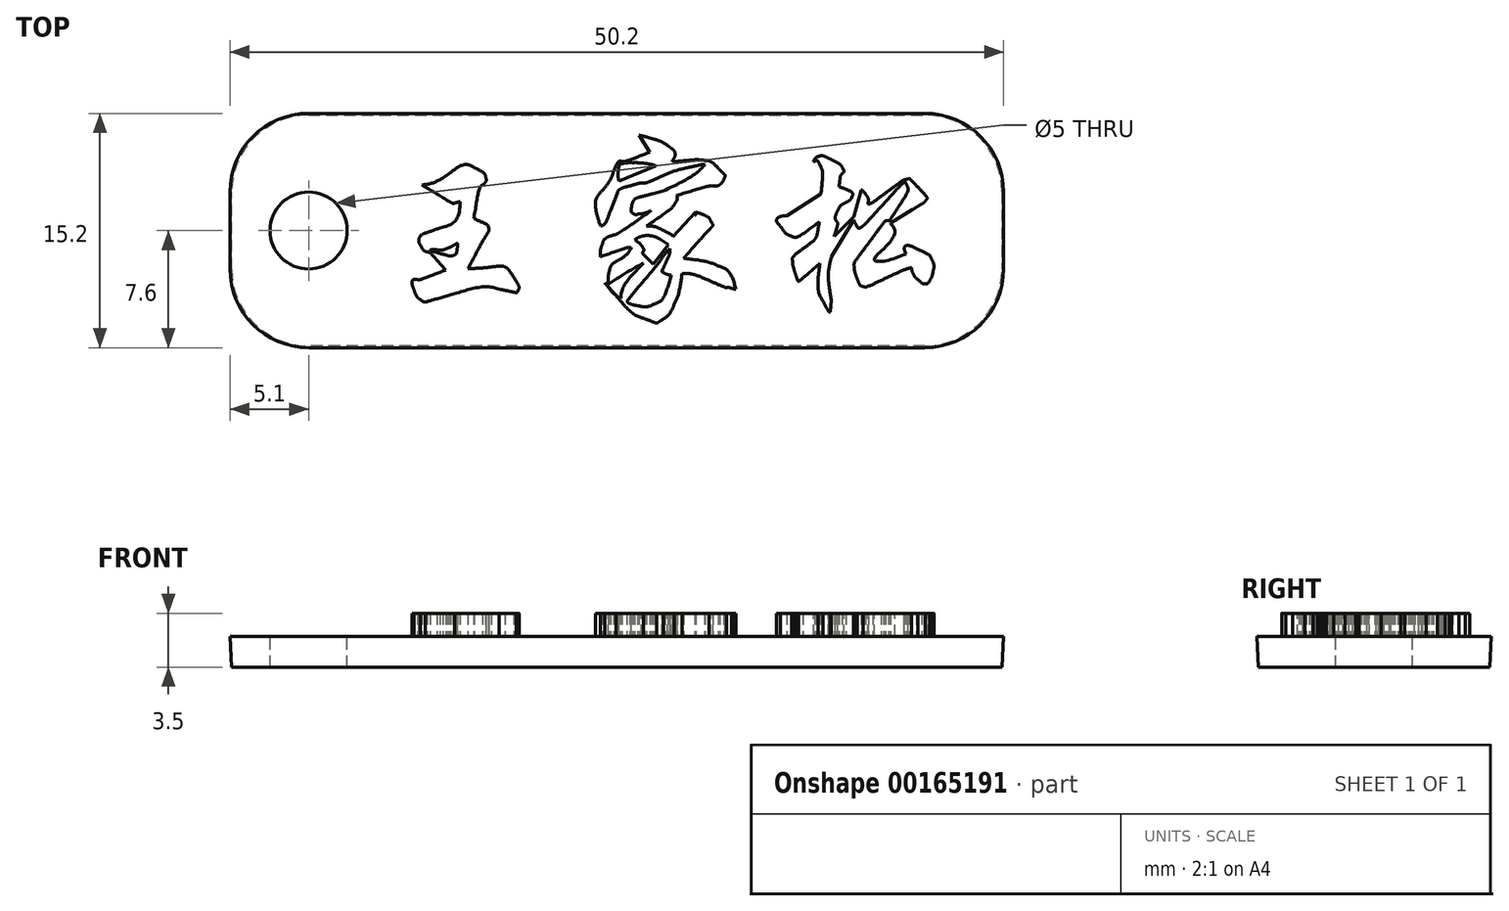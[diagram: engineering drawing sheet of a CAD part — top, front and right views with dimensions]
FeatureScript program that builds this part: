
annotation { "Feature Type Name" : "Feature", "Feature Type Description" : "" }
export const myFeature = defineFeature(function(context is Context, id is Id, definition is map)
    precondition{}
    {
        {
            var Q0;
            Q0=qCreatedBy(makeId("Top.planeOp"),FACE);
            var sketch = newSketch(context, id + "F0", { "sketchPlane" : qUnion([Q0])});
            skLineSegment(sketch, "E0.bottom", {"start": v(20, 7.5) * mm, "end": v(-20, 7.5) * mm});
            skLineSegment(sketch, "E0.top", {"start": v(20, -7.5) * mm, "end": v(-20, -7.5) * mm});
            skLineSegment(sketch, "E0.left", {"start": v(25, 2.5) * mm, "end": v(25, -2.5) * mm});
            skLineSegment(sketch, "E0.right", {"start": v(-25, 2.5) * mm, "end": v(-25, -2.5) * mm});
            skPoint(sketch, "E0.middle", {"position": v(0, 0) * mm});
            skPoint(sketch, "E1.visualSharp", {"position": v(25, 7.5) * mm});
            skArc(sketch, "E1.filletArc", {"start": v(25, 2.5) * mm, "mid": v(23.54, 6.04) * mm, "end": v(20, 7.5) * mm});
            skPoint(sketch, "E2.visualSharp", {"position": v(25, -7.5) * mm});
            skArc(sketch, "E2.filletArc", {"start": v(20, -7.5) * mm, "mid": v(23.54, -6.04) * mm, "end": v(25, -2.5) * mm});
            skPoint(sketch, "E3.visualSharp", {"position": v(-25, 7.5) * mm});
            skArc(sketch, "E3.filletArc", {"start": v(-20, 7.5) * mm, "mid": v(-23.54, 6.04) * mm, "end": v(-25, 2.5) * mm});
            skPoint(sketch, "E4.visualSharp", {"position": v(-25, -7.5) * mm});
            skArc(sketch, "E4.filletArc", {"start": v(-25, -2.5) * mm, "mid": v(-23.54, -6.04) * mm, "end": v(-20, -7.5) * mm});
            skSolve(sketch);
        }
        {
            var Q0;
            Q0=makeQuery(id+"F0.imprint","IMPRINT",FACE,{"disambiguationData":[TD([[makeQuery(id+"F0.imprint","IMPRINT",EDGE,{"derivedFrom":sQuery(id+"F0.wireOp",EDGE,"E0.bottom")}),1.0]])]});
            extrude(context, id + "F1", {"entities" : qUnion([Q0]), "depth" : 2 * mm, "hasDraft" : true, "draftAngle" : 3 * degree});
        }
        {
            var Q0;
            Q0=makeQuery(id+"F1.opExtrude","CAP_FACE",FACE,{"disambiguationData":[OSD([sQuery(id+"F0.wireOp",EDGE,"E0.bottom"),sQuery(id+"F0.wireOp",EDGE,"E0.top"),sQuery(id+"F0.wireOp",EDGE,"E0.left"),sQuery(id+"F0.wireOp",EDGE,"E0.right"),sQuery(id+"F0.wireOp",EDGE,"E1.filletArc"),sQuery(id+"F0.wireOp",EDGE,"E2.filletArc"),sQuery(id+"F0.wireOp",EDGE,"E3.filletArc"),sQuery(id+"F0.wireOp",EDGE,"E4.filletArc")])],"isStart":false});
            var sketch = newSketch(context, id + "F2", { "sketchPlane" : qUnion([Q0])});
            skCircle(sketch, "E5", {"center": v(-20, 0) * mm, "radius": 2.5 * mm});
            skLineSegment(sketch, "E6", {"start": v(-20, 7.6) * mm, "end": v(-20, -7.6) * mm, "construction": true});
            skLineSegment(sketch, "E7", {"start": v(20, -7.6) * mm, "end": v(20, 7.6) * mm, "construction": true});
            skSolve(sketch);
        }
        {
            var Q0;
            Q0=makeQuery(id+"F2.imprint","IMPRINT",FACE,{"disambiguationData":[TD([[makeQuery(id+"F2.imprint","IMPRINT",EDGE,{"derivedFrom":sQuery(id+"F2.wireOp",EDGE,"E5")}),1.0]])]});
            extrude(context, id + "F3", {"entities" : qUnion([Q0]), "operationType" : NewBodyOperationType.REMOVE, "endBound" : BoundingType.THROUGH_ALL, "oppositeDirection" : true, "depth" : 14 * mm});
        }
        {
            var Q0;
            Q0=makeQuery(id+"F2.imprint","IMPRINT",FACE,{"disambiguationData":[TD([[makeQuery(id+"F2.imprint","IMPRINT",EDGE,{"derivedFrom":sQuery(id+"F2.wireOp",EDGE,"E5")}),-1.0]])]});
            var sketch = newSketch(context, id + "F4", { "sketchPlane" : qUnion([Q0])});
            skFitSpline(sketch, "E8", {"points": [v(-6.47, -4.03) * mm, v(-6.47, -4.03) * mm, v(-6.49, -4.03) * mm, v(-6.52, -4.03) * mm, v(-6.47, -4.03) * mm]});
            skFitSpline(sketch, "E9", {"points": [v(-6.52, -4.03) * mm, v(-6.56, -4.03) * mm, v(-6.93, -3.95) * mm, v(-7.65, -3.8) * mm]});
            skFitSpline(sketch, "E10", {"points": [v(-7.65, -3.8) * mm, v(-8.35, -3.65) * mm, v(-9.3, -3.75) * mm, v(-10.53, -4.1) * mm]});
            skFitSpline(sketch, "E11", {"points": [v(-10.53, -4.1) * mm, v(-11.75, -4.45) * mm, v(-12.4, -4.63) * mm, v(-12.44, -4.63) * mm]});
            skFitSpline(sketch, "E12", {"points": [v(-12.44, -4.63) * mm, v(-12.52, -4.63) * mm, v(-12.62, -4.58) * mm, v(-12.75, -4.48) * mm]});
            skFitSpline(sketch, "E13", {"points": [v(-12.75, -4.48) * mm, v(-12.9, -4.37) * mm, v(-13.04, -4.17) * mm, v(-13.15, -3.87) * mm]});
            skFitSpline(sketch, "E14", {"points": [v(-13.15, -3.87) * mm, v(-13.27, -3.56) * mm, v(-13.3, -3.32) * mm, v(-13.22, -3.17) * mm]});
            skFitSpline(sketch, "E15", {"points": [v(-13.22, -3.17) * mm, v(-13.12, -3.17) * mm, v(-13.03, -3.18) * mm, v(-12.94, -3.18) * mm]});
            skFitSpline(sketch, "E16", {"points": [v(-12.94, -3.18) * mm, v(-12.82, -3.2) * mm, v(-12.21, -2.99) * mm, v(-11.1, -2.57) * mm]});
            skFitSpline(sketch, "E17", {"points": [v(-11.1, -2.57) * mm, v(-11.78, -1.8) * mm, v(-12.18, -1.4) * mm, v(-12.3, -1.38) * mm]});
            skFitSpline(sketch, "E18", {"points": [v(-12.3, -1.38) * mm, v(-12.44, -1.35) * mm, v(-12.57, -1.24) * mm, v(-12.69, -1.05) * mm]});
            skFitSpline(sketch, "E19", {"points": [v(-12.69, -1.05) * mm, v(-12.8, -0.86) * mm, v(-12.85, -0.73) * mm, v(-12.85, -0.65) * mm]});
            skFitSpline(sketch, "E20", {"points": [v(-12.85, -0.65) * mm, v(-12.85, -0.57) * mm, v(-12.83, -0.5) * mm, v(-12.78, -0.4) * mm]});
            skFitSpline(sketch, "E21", {"points": [v(-12.78, -0.4) * mm, v(-12.7, -0.3) * mm, v(-12.28, -0.11) * mm, v(-11.49, 0.17) * mm]});
            skFitSpline(sketch, "E22", {"points": [v(-11.49, 0.17) * mm, v(-10.7, 0.43) * mm, v(-10.27, 1) * mm, v(-10.18, 1.88) * mm]});
            skFitSpline(sketch, "E23", {"points": [v(-10.18, 1.88) * mm, v(-10.44, 1.8) * mm, v(-10.6, 1.77) * mm, v(-10.63, 1.77) * mm]});
            skFitSpline(sketch, "E24", {"points": [v(-10.63, 1.77) * mm, v(-10.65, 1.77) * mm, v(-11.33, 2.16) * mm, v(-12.65, 2.96) * mm]});
            skFitSpline(sketch, "E25", {"points": [v(-12.65, 2.96) * mm, v(-12.08, 3.05) * mm, v(-11.47, 3.3) * mm, v(-10.82, 3.74) * mm]});
            skFitSpline(sketch, "E26", {"points": [v(-10.82, 3.74) * mm, v(-10.2, 4.17) * mm, v(-9.69, 4.29) * mm, v(-9.26, 4.08) * mm]});
            skFitSpline(sketch, "E27", {"points": [v(-9.26, 4.08) * mm, v(-8.82, 3.87) * mm, v(-8.56, 3.66) * mm, v(-8.5, 3.47) * mm]});
            skFitSpline(sketch, "E28", {"points": [v(-8.5, 3.47) * mm, v(-8.47, 3.28) * mm, v(-8.54, 3.11) * mm, v(-8.7, 2.97) * mm]});
            skFitSpline(sketch, "E29", {"points": [v(-8.7, 2.97) * mm, v(-8.86, 2.83) * mm, v(-9.06, 2.1) * mm, v(-9.29, 0.78) * mm]});
            skFitSpline(sketch, "E30", {"points": [v(-9.29, 0.78) * mm, v(-8.67, 0.5) * mm, v(-8.35, 0.33) * mm, v(-8.33, 0.23) * mm]});
            skFitSpline(sketch, "E31", {"points": [v(-8.33, 0.23) * mm, v(-8.3, 0.13) * mm, v(-8.29, 0.07) * mm, v(-8.29, 0.04) * mm]});
            skFitSpline(sketch, "E32", {"points": [v(-8.29, 0.04) * mm, v(-8.29, 0) * mm, v(-8.36, -0.14) * mm, v(-8.52, -0.38) * mm]});
            skFitSpline(sketch, "E33", {"points": [v(-8.52, -0.38) * mm, v(-8.65, -0.6) * mm, v(-9.04, -1.3) * mm, v(-9.67, -2.48) * mm]});
            skFitSpline(sketch, "E34", {"points": [v(-9.67, -2.48) * mm, v(-9, -2.45) * mm, v(-8.5, -2.4) * mm, v(-8.16, -2.36) * mm]});
            skFitSpline(sketch, "E35", {"points": [v(-8.16, -2.36) * mm, v(-7.68, -2.31) * mm, v(-7.38, -2.31) * mm, v(-7.26, -2.36) * mm]});
            skFitSpline(sketch, "E36", {"points": [v(-7.26, -2.36) * mm, v(-7.14, -2.42) * mm, v(-6.94, -2.65) * mm, v(-6.69, -3.04) * mm]});
            skFitSpline(sketch, "E37", {"points": [v(-6.69, -3.04) * mm, v(-6.44, -3.44) * mm, v(-6.34, -3.7) * mm, v(-6.38, -3.82) * mm]});
            skFitSpline(sketch, "E38", {"points": [v(-6.38, -3.82) * mm, v(-6.44, -3.96) * mm, v(-6.49, -4.03) * mm, v(-6.52, -4.03) * mm]});
            skFitSpline(sketch, "E39", {"points": [v(-10.8, -1.09) * mm, v(-10.8, -1.09) * mm, v(-10.86, -1.1) * mm, v(-10.97, -1.15) * mm, v(-10.8, -1.09) * mm]});
            skLineSegment(sketch, "E40", {"start": v(-6.52, -4.03) * mm, "end": v(-6.47, -4.03) * mm});
            skFitSpline(sketch, "E41", {"points": [v(-11.68, -1.25) * mm, v(-11.9, -1.23) * mm, v(-12.05, -1.24) * mm, v(-12.12, -1.3) * mm]});
            skFitSpline(sketch, "E42", {"points": [v(-12.12, -1.3) * mm, v(-11.3, -1.53) * mm, v(-10.86, -1.65) * mm, v(-10.8, -1.65) * mm]});
            skFitSpline(sketch, "E43", {"points": [v(-10.8, -1.65) * mm, v(-10.72, -1.65) * mm, v(-10.59, -1.6) * mm, v(-10.41, -1.52) * mm]});
            skFitSpline(sketch, "E44", {"points": [v(-10.41, -1.52) * mm, v(-10.36, -1.17) * mm, v(-10.34, -0.94) * mm, v(-10.35, -0.82) * mm]});
            skFitSpline(sketch, "E45", {"points": [v(-10.35, -0.82) * mm, v(-10.65, -1) * mm, v(-10.86, -1.1) * mm, v(-10.97, -1.15) * mm]});
            skLineSegment(sketch, "E46", {"start": v(-10.97, -1.15) * mm, "end": v(-11.28, -1.28) * mm});
            skLineSegment(sketch, "E47", {"start": v(-11.28, -1.28) * mm, "end": v(-11.68, -1.25) * mm});
            skLineSegment(sketch, "E48", {"start": v(-11.68, -1.25) * mm, "end": v(-10.97, -1.15) * mm});
            skFitSpline(sketch, "E49", {"points": [v(7.6, -3.8) * mm, v(7.6, -3.8) * mm, v(7.54, -3.78) * mm, v(7.43, -3.75) * mm, v(7.6, -3.8) * mm]});
            skFitSpline(sketch, "E50", {"points": [v(7.43, -3.75) * mm, v(7.3, -3.7) * mm, v(7.2, -3.7) * mm, v(7.12, -3.7) * mm]});
            skFitSpline(sketch, "E51", {"points": [v(7.12, -3.7) * mm, v(7.1, -3.7) * mm, v(6.71, -3.55) * mm, v(5.99, -3.25) * mm]});
            skFitSpline(sketch, "E52", {"points": [v(5.99, -3.25) * mm, v(5.3, -2.95) * mm, v(4.72, -2.8) * mm, v(4.23, -2.8) * mm]});
            skFitSpline(sketch, "E53", {"points": [v(4.23, -2.8) * mm, v(4.1, -3.66) * mm, v(3.94, -4.32) * mm, v(3.74, -4.77) * mm]});
            skFitSpline(sketch, "E54", {"points": [v(3.74, -4.77) * mm, v(3.53, -5.22) * mm, v(3.3, -5.54) * mm, v(3.03, -5.73) * mm]});
            skFitSpline(sketch, "E55", {"points": [v(3.03, -5.73) * mm, v(2.77, -5.9) * mm, v(2.62, -6) * mm, v(2.58, -6) * mm]});
            skFitSpline(sketch, "E56", {"points": [v(2.58, -6) * mm, v(2.55, -6) * mm, v(2.26, -5.9) * mm, v(1.73, -5.7) * mm]});
            skFitSpline(sketch, "E57", {"points": [v(1.73, -5.7) * mm, v(1.23, -5.5) * mm, v(0.64, -5.01) * mm, v(-0.05, -4.22) * mm]});
            skFitSpline(sketch, "E58", {"points": [v(-0.05, -4.22) * mm, v(-0.2, -4.1) * mm, v(-0.43, -3.82) * mm, v(-0.77, -3.4) * mm]});
            skFitSpline(sketch, "E59", {"points": [v(-0.77, -3.4) * mm, v(-0.43, -3.8) * mm, v(-0.18, -4.06) * mm, v(-0.04, -4.2) * mm]});
            skFitSpline(sketch, "E60", {"points": [v(-0.04, -4.2) * mm, v(0.06, -4.3) * mm, v(0.16, -4.36) * mm, v(0.24, -4.4) * mm]});
            skFitSpline(sketch, "E61", {"points": [v(0.24, -4.4) * mm, v(0.37, -3.8) * mm, v(0.87, -3.03) * mm, v(1.74, -2.1) * mm]});
            skFitSpline(sketch, "E62", {"points": [v(1.74, -2.1) * mm, v(0.97, -2.53) * mm, v(0.2, -3) * mm, v(-0.56, -3.5) * mm]});
            skFitSpline(sketch, "E63", {"points": [v(-0.56, -3.5) * mm, v(-0.56, -3.12) * mm, v(-0.53, -2.8) * mm, v(-0.46, -2.54) * mm]});
            skFitSpline(sketch, "E64", {"points": [v(-0.46, -2.54) * mm, v(-0.4, -2.31) * mm, v(-0.2, -2.1) * mm, v(0.14, -1.9) * mm]});
            skFitSpline(sketch, "E65", {"points": [v(0.14, -1.9) * mm, v(0.47, -1.7) * mm, v(0.74, -1.43) * mm, v(0.95, -1.1) * mm]});
            skFitSpline(sketch, "E66", {"points": [v(0.95, -1.1) * mm, v(0.76, -1.1) * mm, v(0.1, -1.3) * mm, v(-1.06, -1.7) * mm]});
            skFitSpline(sketch, "E67", {"points": [v(-1.06, -1.7) * mm, v(-1.06, -1.35) * mm, v(-1.01, -1.06) * mm, v(-0.92, -0.84) * mm]});
            skFitSpline(sketch, "E68", {"points": [v(-0.92, -0.84) * mm, v(-0.84, -0.61) * mm, v(-0.61, -0.43) * mm, v(-0.26, -0.3) * mm]});
            skFitSpline(sketch, "E69", {"points": [v(-0.26, -0.3) * mm, v(0.06, -0.19) * mm, v(0.9, 0.35) * mm, v(2.24, 1.3) * mm]});
            skFitSpline(sketch, "E70", {"points": [v(2.24, 1.3) * mm, v(1.92, 1.17) * mm, v(1.71, 1.1) * mm, v(1.6, 1.09) * mm]});
            skFitSpline(sketch, "E71", {"points": [v(1.6, 1.09) * mm, v(1.51, 1.09) * mm, v(1.43, 1.08) * mm, v(1.34, 1.06) * mm]});
            skFitSpline(sketch, "E72", {"points": [v(1.34, 1.06) * mm, v(1.28, 1.03) * mm, v(1.2, 1.04) * mm, v(1.09, 1.09) * mm]});
            skFitSpline(sketch, "E73", {"points": [v(1.09, 1.09) * mm, v(0.98, 1.16) * mm, v(0.93, 1.24) * mm, v(0.95, 1.34) * mm]});
            skFitSpline(sketch, "E74", {"points": [v(0.95, 1.34) * mm, v(0.95, 1.45) * mm, v(0.96, 1.57) * mm, v(0.99, 1.7) * mm]});
            skFitSpline(sketch, "E75", {"points": [v(0.99, 1.7) * mm, v(1.03, 1.83) * mm, v(1.08, 1.93) * mm, v(1.14, 2) * mm]});
            skFitSpline(sketch, "E76", {"points": [v(1.14, 2) * mm, v(1.2, 2.08) * mm, v(1.6, 2.2) * mm, v(2.34, 2.4) * mm]});
            skLineSegment(sketch, "E77", {"start": v(-10.97, -1.15) * mm, "end": v(-10.8, -1.09) * mm});
            skFitSpline(sketch, "E78", {"points": [v(3.04, 2.58) * mm, v(4.32, 3.2) * mm, v(5.22, 3.78) * mm, v(5.73, 4.3) * mm]});
            skFitSpline(sketch, "E79", {"points": [v(5.73, 4.3) * mm, v(5.64, 4.3) * mm, v(5.27, 4.23) * mm, v(4.64, 4.1) * mm]});
            skFitSpline(sketch, "E80", {"points": [v(4.64, 4.1) * mm, v(4, 3.94) * mm, v(3.4, 3.74) * mm, v(2.84, 3.5) * mm]});
            skFitSpline(sketch, "E81", {"points": [v(2.84, 3.5) * mm, v(2.25, 3.23) * mm, v(1.88, 3.1) * mm, v(1.73, 3.1) * mm]});
            skFitSpline(sketch, "E82", {"points": [v(1.73, 3.1) * mm, v(1.6, 3.1) * mm, v(1.3, 3.03) * mm, v(0.83, 2.9) * mm]});
            skFitSpline(sketch, "E83", {"points": [v(0.83, 2.9) * mm, v(0.37, 2.76) * mm, v(0.1, 2.61) * mm, v(0.04, 2.44) * mm]});
            skLineSegment(sketch, "E84", {"start": v(2.34, 2.4) * mm, "end": v(3.04, 2.58) * mm});
            skLineSegment(sketch, "E85", {"start": v(3.04, 2.58) * mm, "end": v(2.34, 2.4) * mm});
            skFitSpline(sketch, "E86", {"points": [v(-0.4, 1.3) * mm, v(-0.64, 0.7) * mm, v(-0.85, 0.36) * mm, v(-1.05, 0.3) * mm]});
            skFitSpline(sketch, "E87", {"points": [v(-1.05, 0.3) * mm, v(-1.24, 0.87) * mm, v(-1.36, 1.32) * mm, v(-1.38, 1.65) * mm]});
            skFitSpline(sketch, "E88", {"points": [v(-1.38, 1.65) * mm, v(-1.38, 1.94) * mm, v(-1.22, 2.27) * mm, v(-0.9, 2.65) * mm]});
            skFitSpline(sketch, "E89", {"points": [v(-0.9, 2.65) * mm, v(-0.6, 3.02) * mm, v(-0.37, 3.42) * mm, v(-0.2, 3.84) * mm]});
            skFitSpline(sketch, "E90", {"points": [v(-0.2, 3.84) * mm, v(-0.02, 4.27) * mm, v(0.15, 4.5) * mm, v(0.33, 4.5) * mm]});
            skFitSpline(sketch, "E91", {"points": [v(0.33, 4.5) * mm, v(0.53, 4.5) * mm, v(1.13, 4.7) * mm, v(2.14, 5.1) * mm]});
            skLineSegment(sketch, "E92", {"start": v(0.04, 2.44) * mm, "end": v(-0.4, 1.3) * mm});
            skLineSegment(sketch, "E93", {"start": v(-0.4, 1.3) * mm, "end": v(0.04, 2.44) * mm});
            skFitSpline(sketch, "E94", {"points": [v(1.43, 6.2) * mm, v(1.8, 6.1) * mm, v(2.1, 6.02) * mm, v(2.37, 5.94) * mm]});
            skFitSpline(sketch, "E95", {"points": [v(2.37, 5.94) * mm, v(2.7, 5.85) * mm, v(3.01, 5.7) * mm, v(3.31, 5.5) * mm]});
            skFitSpline(sketch, "E96", {"points": [v(3.31, 5.5) * mm, v(3.6, 5.3) * mm, v(3.75, 5.14) * mm, v(3.77, 5.04) * mm]});
            skFitSpline(sketch, "E97", {"points": [v(3.77, 5.04) * mm, v(3.8, 4.95) * mm, v(3.75, 4.76) * mm, v(3.6, 4.5) * mm]});
            skLineSegment(sketch, "E98", {"start": v(2.14, 5.1) * mm, "end": v(1.43, 6.2) * mm});
            skLineSegment(sketch, "E99", {"start": v(1.43, 6.2) * mm, "end": v(2.14, 5.1) * mm});
            skFitSpline(sketch, "E100", {"points": [v(5.08, 4.6) * mm, v(5.28, 4.6) * mm, v(5.49, 4.58) * mm, v(5.7, 4.55) * mm]});
            skFitSpline(sketch, "E101", {"points": [v(5.7, 4.55) * mm, v(5.97, 4.53) * mm, v(6.27, 4.36) * mm, v(6.59, 4.04) * mm]});
            skFitSpline(sketch, "E102", {"points": [v(6.59, 4.04) * mm, v(6.89, 3.74) * mm, v(7.04, 3.58) * mm, v(7.04, 3.56) * mm]});
            skFitSpline(sketch, "E103", {"points": [v(7.04, 3.56) * mm, v(7.04, 3.53) * mm, v(7, 3.44) * mm, v(6.93, 3.29) * mm]});
            skFitSpline(sketch, "E104", {"points": [v(6.93, 3.29) * mm, v(6.87, 3.18) * mm, v(6.8, 3.08) * mm, v(6.7, 2.98) * mm]});
            skFitSpline(sketch, "E105", {"points": [v(6.7, 2.98) * mm, v(6.59, 2.91) * mm, v(6.44, 2.89) * mm, v(6.24, 2.9) * mm]});
            skFitSpline(sketch, "E106", {"points": [v(6.24, 2.9) * mm, v(6.06, 2.9) * mm, v(5.28, 2.7) * mm, v(3.9, 2.3) * mm]});
            skFitSpline(sketch, "E107", {"points": [v(3.9, 2.3) * mm, v(3.93, 2.2) * mm, v(3.94, 2.14) * mm, v(3.93, 2.09) * mm]});
            skFitSpline(sketch, "E108", {"points": [v(3.93, 2.09) * mm, v(3.93, 2.03) * mm, v(3.86, 1.9) * mm, v(3.74, 1.7) * mm]});
            skFitSpline(sketch, "E109", {"points": [v(3.74, 1.7) * mm, v(3.62, 1.51) * mm, v(3.01, 1.05) * mm, v(1.93, 0.3) * mm]});
            skFitSpline(sketch, "E110", {"points": [v(1.93, 0.3) * mm, v(2.26, 0.3) * mm, v(2.62, 0.2) * mm, v(3.03, 0) * mm]});
            skFitSpline(sketch, "E111", {"points": [v(3.03, 0) * mm, v(3.43, -0.2) * mm, v(3.63, -0.34) * mm, v(3.63, -0.4) * mm]});
            skLineSegment(sketch, "E112", {"start": v(3.6, 4.5) * mm, "end": v(5.08, 4.6) * mm});
            skLineSegment(sketch, "E113", {"start": v(5.08, 4.6) * mm, "end": v(3.6, 4.5) * mm});
            skFitSpline(sketch, "E114", {"points": [v(5.13, 1.2) * mm, v(5.68, 1) * mm, v(6, 0.82) * mm, v(6.08, 0.65) * mm]});
            skFitSpline(sketch, "E115", {"points": [v(6.08, 0.65) * mm, v(6.14, 0.54) * mm, v(6.2, 0.44) * mm, v(6.24, 0.36) * mm]});
            skFitSpline(sketch, "E116", {"points": [v(6.24, 0.36) * mm, v(6.24, 0.33) * mm, v(6.16, 0.23) * mm, v(5.99, 0.04) * mm]});
            skFitSpline(sketch, "E117", {"points": [v(5.99, 0.04) * mm, v(5.82, -0.12) * mm, v(5.27, -0.74) * mm, v(4.34, -1.8) * mm]});
            skFitSpline(sketch, "E118", {"points": [v(4.34, -1.8) * mm, v(5.34, -1.93) * mm, v(6.1, -2.1) * mm, v(6.59, -2.3) * mm]});
            skFitSpline(sketch, "E119", {"points": [v(6.59, -2.3) * mm, v(7.1, -2.5) * mm, v(7.47, -3) * mm, v(7.73, -3.8) * mm]});
            skFitSpline(sketch, "E120", {"points": [v(7.73, -3.8) * mm, v(7.64, -3.8) * mm, v(7.54, -3.78) * mm, v(7.43, -3.75) * mm]});
            skLineSegment(sketch, "E121", {"start": v(3.63, -0.4) * mm, "end": v(5.13, 1.2) * mm});
            skLineSegment(sketch, "E122", {"start": v(5.13, 1.2) * mm, "end": v(3.63, -0.4) * mm});
            skFitSpline(sketch, "E123", {"points": [v(2.53, 4.2) * mm, v(2.35, 4.26) * mm, v(2.13, 4.32) * mm, v(1.88, 4.35) * mm]});
            skFitSpline(sketch, "E124", {"points": [v(1.88, 4.35) * mm, v(1.68, 4.38) * mm, v(1.4, 4.4) * mm, v(1.04, 4.4) * mm]});
            skFitSpline(sketch, "E125", {"points": [v(1.04, 4.4) * mm, v(0.73, 4.4) * mm, v(0.43, 4.37) * mm, v(0.13, 4.3) * mm]});
            skFitSpline(sketch, "E126", {"points": [v(0.13, 4.3) * mm, v(0.13, 4.12) * mm, v(0.12, 3.97) * mm, v(0.1, 3.85) * mm]});
            skFitSpline(sketch, "E127", {"points": [v(0.1, 3.85) * mm, v(0.07, 3.75) * mm, v(0.08, 3.53) * mm, v(0.14, 3.2) * mm]});
            skLineSegment(sketch, "E128", {"start": v(7.43, -3.75) * mm, "end": v(7.6, -3.8) * mm});
            skFitSpline(sketch, "E129", {"points": [v(5.14, 1) * mm, v(5.14, 1) * mm, v(5.13, 1) * mm, v(5.1, 1) * mm, v(5.14, 1) * mm]});
            skFitSpline(sketch, "E130", {"points": [v(5.1, 1) * mm, v(5.06, 1) * mm, v(4.84, 0.76) * mm, v(4.44, 0.28) * mm]});
            skFitSpline(sketch, "E131", {"points": [v(4.44, 0.28) * mm, v(4.05, -0.18) * mm, v(3.86, -0.47) * mm, v(3.89, -0.6) * mm]});
            skFitSpline(sketch, "E132", {"points": [v(3.89, -0.6) * mm, v(3.93, -0.74) * mm, v(3.98, -0.83) * mm, v(4.04, -0.9) * mm]});
            skFitSpline(sketch, "E133", {"points": [v(4.04, -0.9) * mm, v(4.57, -0.5) * mm, v(4.92, -0.12) * mm, v(5.1, 0.24) * mm]});
            skFitSpline(sketch, "E134", {"points": [v(5.1, 0.24) * mm, v(5.26, 0.61) * mm, v(5.31, 0.83) * mm, v(5.24, 0.9) * mm]});
            skFitSpline(sketch, "E135", {"points": [v(5.24, 0.9) * mm, v(5.18, 0.96) * mm, v(5.13, 1) * mm, v(5.1, 1) * mm]});
            skLineSegment(sketch, "E136", {"start": v(0.14, 3.2) * mm, "end": v(2.53, 4.2) * mm});
            skLineSegment(sketch, "E137", {"start": v(2.53, 4.2) * mm, "end": v(0.14, 3.2) * mm});
            skFitSpline(sketch, "E138", {"points": [v(3.35, -0.9) * mm, v(2.55, -0.44) * mm, v(1.82, -0.33) * mm, v(1.15, -0.59) * mm]});
            skFitSpline(sketch, "E139", {"points": [v(1.15, -0.59) * mm, v(1.42, -0.8) * mm, v(1.6, -0.95) * mm, v(1.65, -1.05) * mm]});
            skFitSpline(sketch, "E140", {"points": [v(1.65, -1.05) * mm, v(1.72, -1.16) * mm, v(1.75, -1.22) * mm, v(1.75, -1.24) * mm]});
            skFitSpline(sketch, "E141", {"points": [v(1.75, -1.24) * mm, v(1.75, -1.27) * mm, v(1.72, -1.36) * mm, v(1.65, -1.5) * mm]});
            skLineSegment(sketch, "E142", {"start": v(5.1, 1) * mm, "end": v(5.14, 1) * mm});
            skFitSpline(sketch, "E143", {"points": [v(3.38, -2.89) * mm, v(3.38, -2.89) * mm, v(3.3, -2.86) * mm, v(3.13, -2.79) * mm, v(3.38, -2.89) * mm]});
            skFitSpline(sketch, "E144", {"points": [v(3.13, -2.79) * mm, v(3, -2.72) * mm, v(2.94, -2.67) * mm, v(2.94, -2.65) * mm]});
            skFitSpline(sketch, "E145", {"points": [v(2.94, -2.65) * mm, v(2.94, -2.61) * mm, v(3.03, -2.41) * mm, v(3.2, -2.05) * mm]});
            skFitSpline(sketch, "E146", {"points": [v(3.2, -2.05) * mm, v(3.37, -1.66) * mm, v(3.45, -1.37) * mm, v(3.45, -1.18) * mm]});
            skFitSpline(sketch, "E147", {"points": [v(3.45, -1.18) * mm, v(3.23, -1.4) * mm, v(3.06, -1.6) * mm, v(2.94, -1.78) * mm]});
            skFitSpline(sketch, "E148", {"points": [v(2.94, -1.78) * mm, v(2.78, -2.02) * mm, v(2.02, -2.95) * mm, v(0.65, -4.6) * mm]});
            skFitSpline(sketch, "E149", {"points": [v(0.65, -4.6) * mm, v(0.78, -4.72) * mm, v(1.03, -4.82) * mm, v(1.4, -4.88) * mm]});
            skFitSpline(sketch, "E150", {"points": [v(1.4, -4.88) * mm, v(1.77, -4.95) * mm, v(2.14, -4.9) * mm, v(2.5, -4.73) * mm]});
            skFitSpline(sketch, "E151", {"points": [v(2.5, -4.73) * mm, v(2.86, -4.57) * mm, v(3.21, -3.96) * mm, v(3.54, -2.89) * mm]});
            skFitSpline(sketch, "E152", {"points": [v(3.54, -2.89) * mm, v(3.43, -2.89) * mm, v(3.3, -2.86) * mm, v(3.13, -2.79) * mm]});
            skLineSegment(sketch, "E153", {"start": v(1.65, -1.5) * mm, "end": v(2.35, -2.2) * mm});
            skLineSegment(sketch, "E154", {"start": v(2.35, -2.2) * mm, "end": v(3.35, -0.9) * mm});
            skLineSegment(sketch, "E155", {"start": v(3.35, -0.9) * mm, "end": v(1.65, -1.5) * mm});
            skFitSpline(sketch, "E156", {"points": [v(20.45, -3.02) * mm, v(20.45, -3.02) * mm, v(20.4, -3.1) * mm, v(20.31, -3.25) * mm, v(20.45, -3.02) * mm]});
            skFitSpline(sketch, "E157", {"points": [v(20.31, -3.25) * mm, v(20.22, -3.4) * mm, v(20.12, -3.46) * mm, v(20.02, -3.46) * mm]});
            skFitSpline(sketch, "E158", {"points": [v(20.02, -3.46) * mm, v(19.92, -3.46) * mm, v(19.76, -3.37) * mm, v(19.54, -3.18) * mm]});
            skFitSpline(sketch, "E159", {"points": [v(19.54, -3.18) * mm, v(19.34, -2.99) * mm, v(19.2, -2.73) * mm, v(19.12, -2.4) * mm]});
            skFitSpline(sketch, "E160", {"points": [v(19.12, -2.4) * mm, v(18.82, -2.49) * mm, v(18.24, -2.73) * mm, v(17.4, -3.12) * mm]});
            skFitSpline(sketch, "E161", {"points": [v(17.4, -3.12) * mm, v(16.6, -3.5) * mm, v(16.13, -3.67) * mm, v(15.99, -3.63) * mm]});
            skFitSpline(sketch, "E162", {"points": [v(15.99, -3.63) * mm, v(15.85, -3.6) * mm, v(15.72, -3.44) * mm, v(15.6, -3.15) * mm]});
            skFitSpline(sketch, "E163", {"points": [v(15.6, -3.15) * mm, v(15.5, -2.85) * mm, v(15.43, -2.6) * mm, v(15.41, -2.42) * mm]});
            skFitSpline(sketch, "E164", {"points": [v(15.41, -2.42) * mm, v(15.4, -2.2) * mm, v(15.45, -2.02) * mm, v(15.58, -1.85) * mm]});
            skFitSpline(sketch, "E165", {"points": [v(15.58, -1.85) * mm, v(15.78, -1.57) * mm, v(16.12, -1.1) * mm, v(16.62, -0.45) * mm]});
            skFitSpline(sketch, "E166", {"points": [v(16.62, -0.45) * mm, v(17.18, 0.32) * mm, v(17.52, 0.66) * mm, v(17.65, 0.56) * mm]});
            skFitSpline(sketch, "E167", {"points": [v(17.65, 0.56) * mm, v(18.52, 1.9) * mm, v(18.92, 2.67) * mm, v(18.84, 2.88) * mm]});
            skFitSpline(sketch, "E168", {"points": [v(18.84, 2.88) * mm, v(18.76, 3.08) * mm, v(18.7, 3.15) * mm, v(18.62, 3.1) * mm]});
            skFitSpline(sketch, "E169", {"points": [v(18.62, 3.1) * mm, v(18.55, 3.07) * mm, v(18.06, 2.55) * mm, v(17.15, 1.55) * mm]});
            skFitSpline(sketch, "E170", {"points": [v(17.15, 1.55) * mm, v(16.23, 0.54) * mm, v(15.7, 0.15) * mm, v(15.55, 0.36) * mm]});
            skFitSpline(sketch, "E171", {"points": [v(15.55, 0.36) * mm, v(15.47, 0.49) * mm, v(15.41, 0.6) * mm, v(15.39, 0.7) * mm]});
            skLineSegment(sketch, "E172", {"start": v(3.13, -2.79) * mm, "end": v(3.38, -2.89) * mm});
            skFitSpline(sketch, "E173", {"points": [v(13.93, -1.7) * mm, v(13.8, -2.3) * mm, v(13.73, -2.75) * mm, v(13.74, -3.06) * mm]});
            skFitSpline(sketch, "E174", {"points": [v(13.74, -3.06) * mm, v(13.75, -3.31) * mm, v(13.78, -3.6) * mm, v(13.84, -3.95) * mm]});
            skLineSegment(sketch, "E175", {"start": v(15.39, 0.7) * mm, "end": v(13.93, -1.7) * mm});
            skLineSegment(sketch, "E176", {"start": v(13.93, -1.7) * mm, "end": v(15.39, 0.7) * mm});
            skFitSpline(sketch, "E177", {"points": [v(13.87, -5.3) * mm, v(13.8, -5.3) * mm, v(13.64, -5.05) * mm, v(13.38, -4.56) * mm]});
            skFitSpline(sketch, "E178", {"points": [v(13.38, -4.56) * mm, v(13.12, -4.08) * mm, v(13.06, -3.26) * mm, v(13.19, -2.12) * mm]});
            skFitSpline(sketch, "E179", {"points": [v(13.19, -2.12) * mm, v(12.28, -2.9) * mm, v(11.82, -3.3) * mm, v(11.8, -3.3) * mm]});
            skFitSpline(sketch, "E180", {"points": [v(11.8, -3.3) * mm, v(11.77, -3.3) * mm, v(11.7, -3.12) * mm, v(11.58, -2.76) * mm]});
            skFitSpline(sketch, "E181", {"points": [v(11.58, -2.76) * mm, v(11.46, -2.38) * mm, v(11.4, -2.11) * mm, v(11.4, -1.97) * mm]});
            skFitSpline(sketch, "E182", {"points": [v(11.4, -1.97) * mm, v(11.4, -1.79) * mm, v(11.62, -1.53) * mm, v(12.09, -1.18) * mm]});
            skFitSpline(sketch, "E183", {"points": [v(12.09, -1.18) * mm, v(12.57, -0.83) * mm, v(12.84, -0.6) * mm, v(12.9, -0.48) * mm]});
            skFitSpline(sketch, "E184", {"points": [v(12.9, -0.48) * mm, v(12.97, -0.4) * mm, v(13.05, -0.04) * mm, v(13.15, 0.58) * mm]});
            skFitSpline(sketch, "E185", {"points": [v(13.15, 0.58) * mm, v(12.19, -0.14) * mm, v(11.59, -0.45) * mm, v(11.36, -0.37) * mm]});
            skFitSpline(sketch, "E186", {"points": [v(11.36, -0.37) * mm, v(11.12, -0.28) * mm, v(10.87, -0.07) * mm, v(10.62, 0.28) * mm]});
            skFitSpline(sketch, "E187", {"points": [v(10.62, 0.28) * mm, v(10.36, 0.64) * mm, v(10.5, 0.87) * mm, v(11.03, 0.96) * mm]});
            skLineSegment(sketch, "E188", {"start": v(13.84, -3.95) * mm, "end": v(13.93, -4.49) * mm});
            skLineSegment(sketch, "E189", {"start": v(13.93, -4.49) * mm, "end": v(13.87, -5.3) * mm});
            skLineSegment(sketch, "E190", {"start": v(13.87, -5.3) * mm, "end": v(13.84, -3.95) * mm});
            skFitSpline(sketch, "E191", {"points": [v(13.25, 2.4) * mm, v(13.35, 3.33) * mm, v(13.33, 3.93) * mm, v(13.21, 4.18) * mm]});
            skFitSpline(sketch, "E192", {"points": [v(13.21, 4.18) * mm, v(13.1, 4.44) * mm, v(12.99, 4.55) * mm, v(12.9, 4.52) * mm]});
            skFitSpline(sketch, "E193", {"points": [v(12.9, 4.52) * mm, v(12.8, 4.48) * mm, v(12.78, 4.51) * mm, v(12.83, 4.6) * mm]});
            skFitSpline(sketch, "E194", {"points": [v(12.83, 4.6) * mm, v(12.9, 4.72) * mm, v(13, 4.79) * mm, v(13.14, 4.82) * mm]});
            skFitSpline(sketch, "E195", {"points": [v(13.14, 4.82) * mm, v(13.27, 4.87) * mm, v(13.52, 4.8) * mm, v(13.9, 4.62) * mm]});
            skFitSpline(sketch, "E196", {"points": [v(13.9, 4.62) * mm, v(14.27, 4.44) * mm, v(14.5, 4.27) * mm, v(14.62, 4.1) * mm]});
            skFitSpline(sketch, "E197", {"points": [v(14.62, 4.1) * mm, v(14.72, 3.94) * mm, v(14.73, 3.8) * mm, v(14.63, 3.7) * mm]});
            skFitSpline(sketch, "E198", {"points": [v(14.63, 3.7) * mm, v(14.55, 3.6) * mm, v(14.48, 3.32) * mm, v(14.43, 2.84) * mm]});
            skFitSpline(sketch, "E199", {"points": [v(14.43, 2.84) * mm, v(15.04, 2.61) * mm, v(15.32, 2.41) * mm, v(15.27, 2.24) * mm]});
            skFitSpline(sketch, "E200", {"points": [v(15.27, 2.24) * mm, v(15.21, 2.08) * mm, v(15.08, 1.94) * mm, v(14.86, 1.82) * mm]});
            skFitSpline(sketch, "E201", {"points": [v(14.86, 1.82) * mm, v(14.62, 1.7) * mm, v(14.44, 1.5) * mm, v(14.31, 1.24) * mm]});
            skFitSpline(sketch, "E202", {"points": [v(14.31, 1.24) * mm, v(14.2, 0.97) * mm, v(14.17, 0.76) * mm, v(14.25, 0.63) * mm]});
            skFitSpline(sketch, "E203", {"points": [v(14.25, 0.63) * mm, v(14.33, 0.5) * mm, v(14.28, 0.18) * mm, v(14.1, -0.37) * mm]});
            skLineSegment(sketch, "E204", {"start": v(11.03, 0.96) * mm, "end": v(13.25, 2.4) * mm});
            skLineSegment(sketch, "E205", {"start": v(13.25, 2.4) * mm, "end": v(11.03, 0.96) * mm});
            skFitSpline(sketch, "E206", {"points": [v(15.85, 2.62) * mm, v(15.92, 2.62) * mm, v(16.01, 2.54) * mm, v(16.14, 2.37) * mm]});
            skFitSpline(sketch, "E207", {"points": [v(16.14, 2.37) * mm, v(16.27, 2.18) * mm, v(16.33, 2.02) * mm, v(16.32, 1.88) * mm]});
            skFitSpline(sketch, "E208", {"points": [v(16.32, 1.88) * mm, v(16.34, 1.71) * mm, v(16.71, 1.9) * mm, v(17.45, 2.44) * mm]});
            skFitSpline(sketch, "E209", {"points": [v(17.45, 2.44) * mm, v(18.22, 3) * mm, v(18.65, 3.3) * mm, v(18.73, 3.31) * mm]});
            skLineSegment(sketch, "E210", {"start": v(14.1, -0.37) * mm, "end": v(15.39, 0.88) * mm});
            skLineSegment(sketch, "E211", {"start": v(15.39, 0.88) * mm, "end": v(15.85, 2.62) * mm});
            skLineSegment(sketch, "E212", {"start": v(15.85, 2.62) * mm, "end": v(14.1, -0.37) * mm});
            skFitSpline(sketch, "E213", {"points": [v(18.96, 3.38) * mm, v(19, 3.38) * mm, v(19.2, 3.17) * mm, v(19.6, 2.76) * mm]});
            skFitSpline(sketch, "E214", {"points": [v(19.6, 2.76) * mm, v(19.98, 2.35) * mm, v(20.14, 2.1) * mm, v(20.08, 2) * mm]});
            skFitSpline(sketch, "E215", {"points": [v(20.08, 2) * mm, v(20.01, 1.9) * mm, v(19.92, 1.8) * mm, v(19.8, 1.73) * mm]});
            skFitSpline(sketch, "E216", {"points": [v(19.8, 1.73) * mm, v(19.8, 1.73) * mm, v(19.6, 1.6) * mm, v(19.2, 1.36) * mm]});
            skLineSegment(sketch, "E217", {"start": v(18.73, 3.31) * mm, "end": v(18.96, 3.38) * mm});
            skLineSegment(sketch, "E218", {"start": v(18.96, 3.38) * mm, "end": v(18.73, 3.31) * mm});
            skFitSpline(sketch, "E219", {"points": [v(17.75, 0.47) * mm, v(18.04, 0.06) * mm, v(17.9, -0.5) * mm, v(17.3, -1.2) * mm]});
            skFitSpline(sketch, "E220", {"points": [v(17.3, -1.2) * mm, v(16.72, -1.9) * mm, v(17.2, -2) * mm, v(18.76, -1.53) * mm]});
            skFitSpline(sketch, "E221", {"points": [v(18.76, -1.53) * mm, v(18.67, -1.07) * mm, v(18.9, -0.96) * mm, v(19.44, -1.19) * mm]});
            skFitSpline(sketch, "E222", {"points": [v(19.44, -1.19) * mm, v(20, -1.43) * mm, v(20.33, -1.66) * mm, v(20.44, -1.88) * mm]});
            skFitSpline(sketch, "E223", {"points": [v(20.44, -1.88) * mm, v(20.55, -2.1) * mm, v(20.58, -2.36) * mm, v(20.53, -2.63) * mm]});
            skFitSpline(sketch, "E224", {"points": [v(20.53, -2.63) * mm, v(20.48, -2.89) * mm, v(20.4, -3.1) * mm, v(20.31, -3.25) * mm]});
            skLineSegment(sketch, "E225", {"start": v(19.2, 1.36) * mm, "end": v(17.75, 0.47) * mm});
            skLineSegment(sketch, "E226", {"start": v(17.75, 0.47) * mm, "end": v(19.2, 1.36) * mm});
            skLineSegment(sketch, "E227", {"start": v(20.31, -3.25) * mm, "end": v(20.45, -3.02) * mm});
            skSolve(sketch);
        }
        {
            var Q0;
            Q0=makeQuery(id+"F4.imprint","IMPRINT",FACE,{"disambiguationData":[TD([[makeQuery(id+"F4.imprint","IMPRINT",EDGE,{"derivedFrom":sQuery(id+"F4.wireOp",EDGE,"E157")}),-1.0]])]});
            var Q1;
            Q1=makeQuery(id+"F4.imprint","IMPRINT",FACE,{"disambiguationData":[TD([[makeQuery(id+"F4.imprint","IMPRINT",EDGE,{"derivedFrom":sQuery(id+"F4.wireOp",EDGE,"E9")}),-1.0]])]});
            var Q2;
            Q2=makeQuery(id+"F4.imprint","IMPRINT",FACE,{"disambiguationData":[TD([[makeQuery(id+"F4.imprint","IMPRINT",EDGE,{"derivedFrom":sQuery(id+"F4.wireOp",EDGE,"E50")}),-1.0]])]});
            var Q3;
            Q3=makeQuery(id+"F4.imprint","IMPRINT",FACE,{"disambiguationData":[TD([[makeQuery(id+"F4.imprint","IMPRINT",EDGE,{"derivedFrom":sQuery(id+"F4.wireOp",EDGE,"E130")}),1.0]])]});
            var Q4;
            Q4=makeQuery(id+"F4.imprint","IMPRINT",FACE,{"disambiguationData":[TD([[makeQuery(id+"F4.imprint","IMPRINT",EDGE,{"derivedFrom":sQuery(id+"F4.wireOp",EDGE,"E188")}),-1.0]])]});
            var Q5;
            Q5=makeQuery(id+"F4.imprint","IMPRINT",FACE,{"disambiguationData":[TD([[makeQuery(id+"F4.imprint","IMPRINT",EDGE,{"derivedFrom":sQuery(id+"F4.wireOp",EDGE,"E46")}),-1.0]])]});
            extrude(context, id + "F5", {"entities" : qUnion([Q0, Q1, Q2, Q3, Q4, Q5]), "operationType" : NewBodyOperationType.ADD, "depth" : 1.5 * mm});
        }
    });
